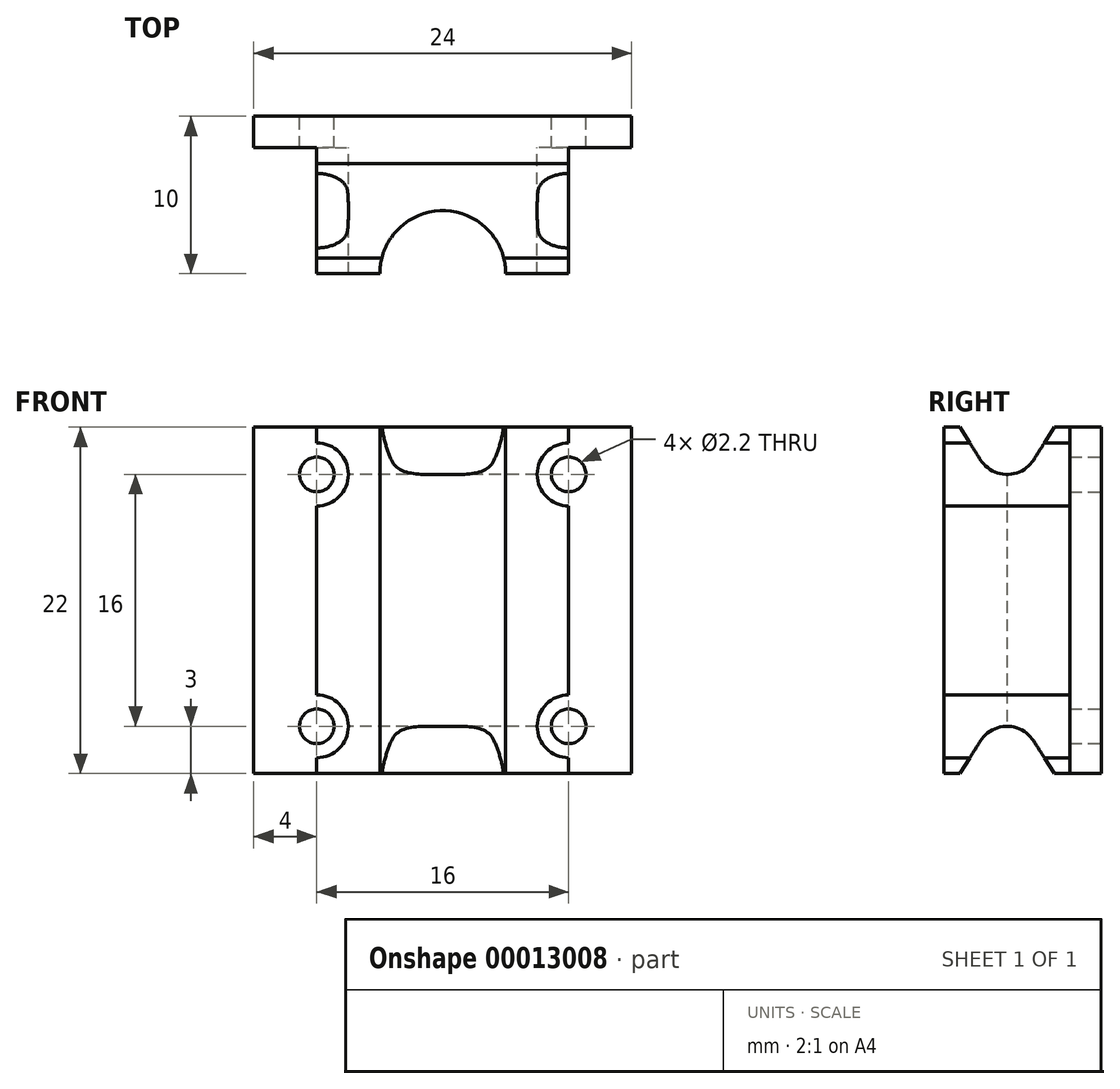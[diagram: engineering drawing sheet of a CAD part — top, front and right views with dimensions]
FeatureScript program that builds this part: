
annotation { "Feature Type Name" : "Feature", "Feature Type Description" : "" }
export const myFeature = defineFeature(function(context is Context, id is Id, definition is map)
    precondition{}
    {
        {
            var Q0;
            Q0=qCreatedBy(makeId("Top.planeOp"),FACE);
            var sketch = newSketch(context, id + "F0", { "sketchPlane" : qUnion([Q0])});
            skArc(sketch, "E0", {"start": v(8, 0) * mm, "mid": v(0, 8) * mm, "end": v(-8, 0) * mm});
            skArc(sketch, "E1", {"start": v(4, 0) * mm, "mid": v(0, 4) * mm, "end": v(-4, 0) * mm});
            skLineSegment(sketch, "E2.bottom", {"start": v(-12, 10) * mm, "end": v(12, 10) * mm});
            skLineSegment(sketch, "E2.top", {"start": v(-12, 8) * mm, "end": v(12, 8) * mm});
            skLineSegment(sketch, "E2.left", {"start": v(-12, 10) * mm, "end": v(-12, 8) * mm});
            skLineSegment(sketch, "E2.right", {"start": v(12, 10) * mm, "end": v(12, 8) * mm});
            skPoint(sketch, "E3", {"position": v(0, 10) * mm});
            skLineSegment(sketch, "E4", {"start": v(-8, 0) * mm, "end": v(-8, 8) * mm});
            skLineSegment(sketch, "E5", {"start": v(8, 0) * mm, "end": v(8, 8) * mm});
            skLineSegment(sketch, "E6", {"start": v(-8, 0) * mm, "end": v(-4, 0) * mm});
            skLineSegment(sketch, "E7.trimOffspring", {"start": v(4, 0) * mm, "end": v(8, 0) * mm});
            skSolve(sketch);
        }
        {
            var Q0;
            Q0 = qSketchRegion(id + "F0", true);
            extrude(context, id + "F1", {"entities" : qUnion([Q0]), "depth" : 22 * mm});
        }
        {
            var Q0;
            Q0=makeQuery(id+"F1.opExtrude","SWEPT_FACE",FACE,{"disambiguationData":[OSD([sQuery(id+"F0.wireOp",EDGE,"E4")])]});
            var sketch = newSketch(context, id + "F2", { "sketchPlane" : qUnion([Q0])});
            skLineSegment(sketch, "E8", {"start": v(-7, 0) * mm, "end": v(-5.69, 2.07) * mm});
            skLineSegment(sketch, "E9", {"start": v(-1, 0) * mm, "end": v(-2.31, 2.07) * mm});
            skArc(sketch, "E10", {"start": v(-2.31, 2.07) * mm, "mid": v(-4, 3) * mm, "end": v(-5.69, 2.07) * mm});
            skLineSegment(sketch, "E11", {"start": v(0, 11) * mm, "end": v(-8, 11) * mm, "construction": true});
            skLineSegment(sketch, "E12.MirrorCS", {"start": v(-1, 22) * mm, "end": v(-2.31, 19.93) * mm});
            skLineSegment(sketch, "E13.MirrorCS", {"start": v(-7, 22) * mm, "end": v(-5.69, 19.93) * mm});
            skArc(sketch, "E14.MirrorCS", {"start": v(-2.31, 19.93) * mm, "mid": v(-4, 19) * mm, "end": v(-5.69, 19.93) * mm});
            skSolve(sketch);
        }
        {
            var Q0;
            Q0=makeQuery(id+"F2.imprint","IMPRINT",FACE,{"disambiguationData":[TD([[makeQuery(id+"F2.imprint","IMPRINT",EDGE,{"derivedFrom":sQuery(id+"F2.wireOp",EDGE,"E12.MirrorCS")}),-1.0]])]});
            var Q1;
            Q1=makeQuery(id+"F2.imprint","IMPRINT",FACE,{"disambiguationData":[TD([[makeQuery(id+"F2.imprint","IMPRINT",EDGE,{"derivedFrom":sQuery(id+"F2.wireOp",EDGE,"E8")}),-1.0]])]});
            extrude(context, id + "F3", {"entities" : qUnion([Q0, Q1]), "operationType" : NewBodyOperationType.REMOVE, "endBound" : BoundingType.THROUGH_ALL, "oppositeDirection" : true, "depth" : 25 * mm});
        }
        {
            var Q0;
            Q0=makeQuery(id+"F1.opExtrude","SWEPT_FACE",FACE,{"disambiguationData":[OSD([sQuery(id+"F0.wireOp",EDGE,"E2.bottom")])]});
            var sketch = newSketch(context, id + "F4", { "sketchPlane" : qUnion([Q0])});
            skCircle(sketch, "E15", {"center": v(8, 19) * mm, "radius": 1.1 * mm});
            skCircle(sketch, "E16", {"center": v(-8, 19) * mm, "radius": 1.1 * mm});
            skCircle(sketch, "E17", {"center": v(-8, 3) * mm, "radius": 1.1 * mm});
            skCircle(sketch, "E18", {"center": v(8, 3) * mm, "radius": 1.1 * mm});
            skLineSegment(sketch, "E19.rect.bottom", {"start": v(-8, 19) * mm, "end": v(8, 19) * mm, "construction": true});
            skLineSegment(sketch, "E19.rect.top", {"start": v(-8, 3) * mm, "end": v(8, 3) * mm, "construction": true});
            skLineSegment(sketch, "E19.rect.left", {"start": v(-8, 19) * mm, "end": v(-8, 3) * mm, "construction": true});
            skLineSegment(sketch, "E19.rect.right", {"start": v(8, 19) * mm, "end": v(8, 3) * mm, "construction": true});
            skPoint(sketch, "E19.rect.middle", {"position": v(0, 11) * mm});
            skPoint(sketch, "E20", {"position": v(12, 11) * mm});
            skSolve(sketch);
        }
        {
            var Q0;
            Q0=makeQuery(id+"F4.imprint","IMPRINT",FACE,{"disambiguationData":[TD([[makeQuery(id+"F4.imprint","IMPRINT",EDGE,{"derivedFrom":sQuery(id+"F4.wireOp",EDGE,"fa18feeb-89b5-4b1f-9c55-68bb746665c7")}),1.0]])]});
            var Q1;
            Q1=makeQuery(id+"F4.imprint","IMPRINT",FACE,{"disambiguationData":[TD([[makeQuery(id+"F4.imprint","IMPRINT",EDGE,{"derivedFrom":sQuery(id+"F4.wireOp",EDGE,"35875b48-3d4a-4871-9f73-26c4418eb738")}),1.0]])]});
            var Q2;
            Q2=makeQuery(id+"F4.imprint","IMPRINT",FACE,{"disambiguationData":[TD([[makeQuery(id+"F4.imprint","IMPRINT",EDGE,{"derivedFrom":sQuery(id+"F4.wireOp",EDGE,"E16")}),1.0]])]});
            var Q3;
            Q3=makeQuery(id+"F4.imprint","IMPRINT",FACE,{"disambiguationData":[TD([[makeQuery(id+"F4.imprint","IMPRINT",EDGE,{"derivedFrom":sQuery(id+"F4.wireOp",EDGE,"E15")}),1.0]])]});
            var Q4;
            Q4=makeQuery(id+"F4.imprint","IMPRINT",FACE,{"disambiguationData":[TD([[makeQuery(id+"F4.imprint","IMPRINT",EDGE,{"derivedFrom":sQuery(id+"F4.wireOp",EDGE,"E18")}),1.0]])]});
            var Q5;
            Q5=makeQuery(id+"F4.imprint","IMPRINT",FACE,{"disambiguationData":[TD([[makeQuery(id+"F4.imprint","IMPRINT",EDGE,{"derivedFrom":sQuery(id+"F4.wireOp",EDGE,"E17")}),1.0]])]});
            extrude(context, id + "F5", {"entities" : qUnion([Q0, Q1, Q2, Q3, Q4, Q5]), "operationType" : NewBodyOperationType.REMOVE, "endBound" : BoundingType.THROUGH_ALL, "oppositeDirection" : true, "depth" : 25 * mm});
        }
        {
            var Q0;
            {var subQ0=sQuery(id+"F0.wireOp",EDGE,"E2.top");Q0=makeQuery(id+"F1.opExtrude","SWEPT_FACE",FACE,{"disambiguationData":[OSD([subQ0]),TDD([makeQuery(id+"F0.imprint","IMPRINT",EDGE,{"disambiguationData":[TD([[makeQuery(id+"F0.imprint","INTERSECT",VERTEX,{"derivedFrom":[subQ0,sQuery(id+"F0.wireOp",EDGE,"E2.right")]}),1.0]])],"derivedFrom":subQ0})])]});}
            var sketch = newSketch(context, id + "F6", { "sketchPlane" : qUnion([Q0])});
            skCircle(sketch, "E21", {"center": v(8, 19) * mm, "radius": 2 * mm});
            skCircle(sketch, "E22", {"center": v(8, 3) * mm, "radius": 2 * mm});
            skSolve(sketch);
        }
        {
            var Q0;
            Q0 = qSketchRegion(id + "F6", true);
            extrude(context, id + "F7", {"entities" : qUnion([Q0]), "operationType" : NewBodyOperationType.REMOVE, "depth" : 25 * mm});
        }
        {
            var Q0;
            {var subQ0=sQuery(id+"F0.wireOp",EDGE,"E2.top");Q0=makeQuery(id+"F1.opExtrude","SWEPT_FACE",FACE,{"disambiguationData":[OSD([subQ0]),TDD([makeQuery(id+"F0.imprint","IMPRINT",EDGE,{"disambiguationData":[TD([[makeQuery(id+"F0.imprint","INTERSECT",VERTEX,{"derivedFrom":[subQ0,sQuery(id+"F0.wireOp",EDGE,"E2.left")]}),-1.0]])],"derivedFrom":subQ0})])]});}
            var sketch = newSketch(context, id + "F8", { "sketchPlane" : qUnion([Q0])});
            skCircle(sketch, "E23", {"center": v(-8, 19) * mm, "radius": 2 * mm});
            skCircle(sketch, "E24", {"center": v(-8, 3) * mm, "radius": 2 * mm});
            skSolve(sketch);
        }
        {
            var Q0;
            Q0 = qSketchRegion(id + "F8", true);
            extrude(context, id + "F9", {"entities" : qUnion([Q0]), "operationType" : NewBodyOperationType.REMOVE, "depth" : 25 * mm});
        }
    });
